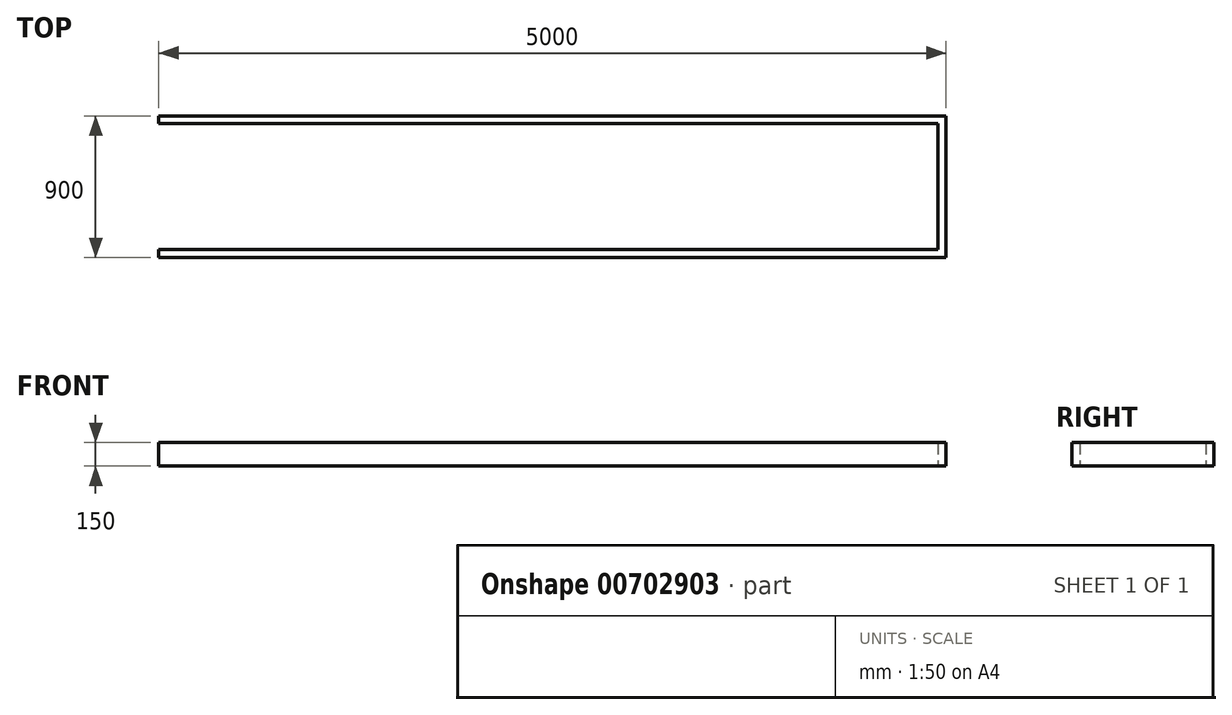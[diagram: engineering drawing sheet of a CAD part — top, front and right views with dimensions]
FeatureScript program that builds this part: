
annotation { "Feature Type Name" : "Feature", "Feature Type Description" : "" }
export const myFeature = defineFeature(function(context is Context, id is Id, definition is map)
    precondition{}
    {
        {
            var Q0;
            Q0=qCreatedBy(makeId("Top.planeOp"),FACE);
            var sketch = newSketch(context, id + "F0", { "sketchPlane" : qUnion([Q0])});
            skLineSegment(sketch, "E0.bottom", {"start": v(0, 0) * mm, "end": v(5000, 0) * mm});
            skLineSegment(sketch, "E0.top", {"start": v(0, -50) * mm, "end": v(5000, -50) * mm});
            skLineSegment(sketch, "E0.left", {"start": v(0, 0) * mm, "end": v(0, -50) * mm});
            skLineSegment(sketch, "E0.right", {"start": v(5000, 0) * mm, "end": v(5000, -50) * mm});
            skLineSegment(sketch, "E1.bottom", {"start": v(0, 4150) * mm, "end": v(5000, 4150) * mm});
            skLineSegment(sketch, "E1.top", {"start": v(0, -900) * mm, "end": v(5000, -900) * mm});
            skLineSegment(sketch, "E1.left", {"start": v(0, -850) * mm, "end": v(0, -900) * mm});
            skLineSegment(sketch, "E1.right", {"start": v(5000, -850) * mm, "end": v(5000, -900) * mm});
            skLineSegment(sketch, "E2.bottom", {"start": v(0, -50) * mm, "end": v(50, -50) * mm});
            skLineSegment(sketch, "E2.top", {"start": v(0, -850) * mm, "end": v(50, -850) * mm});
            skLineSegment(sketch, "E2.left", {"start": v(0, -50) * mm, "end": v(0, -850) * mm});
            skLineSegment(sketch, "E2.right", {"start": v(50, -50) * mm, "end": v(50, -850) * mm});
            skLineSegment(sketch, "E3.bottom", {"start": v(408.44, 5081.05) * mm, "end": v(458.44, 5081.05) * mm});
            skLineSegment(sketch, "E3.top", {"start": v(408.44, 4281.05) * mm, "end": v(458.44, 4281.05) * mm});
            skLineSegment(sketch, "E3.left", {"start": v(408.44, 5081.05) * mm, "end": v(408.44, 4281.05) * mm});
            skLineSegment(sketch, "E3.right", {"start": v(458.44, 5081.05) * mm, "end": v(458.44, 4281.05) * mm});
            skLineSegment(sketch, "E4", {"start": v(5000, -850) * mm, "end": v(0, -850) * mm});
            skLineSegment(sketch, "E5", {"start": v(5000, -50) * mm, "end": v(5000, -850) * mm});
            skLineSegment(sketch, "E6", {"start": v(5000, -850) * mm, "end": v(4950, -850) * mm});
            skLineSegment(sketch, "E7", {"start": v(4950, -850) * mm, "end": v(4950, -50) * mm});
            skLineSegment(sketch, "E8", {"start": v(4950, -50) * mm, "end": v(5000, -50) * mm});
            skLineSegment(sketch, "E9", {"start": v(4950, -450) * mm, "end": v(4950, -500) * mm});
            skSolve(sketch);
        }
        {
            var Q0;
            Q0=makeQuery(id+"F0.imprint","IMPRINT",FACE,{"disambiguationData":[TD([[makeQuery(id+"F0.imprint","IMPRINT",EDGE,{"derivedFrom":sQuery(id+"F0.wireOp",EDGE,"E0.bottom")}),-1.0]])]});
            var Q1;
            Q1=makeQuery(id+"F0.imprint","IMPRINT",FACE,{"disambiguationData":[TD([[makeQuery(id+"F0.imprint","IMPRINT",EDGE,{"derivedFrom":sQuery(id+"F0.wireOp",EDGE,"E2.bottom")}),-1.0]])]});
            var Q2;
            Q2=makeQuery(id+"F0.imprint","IMPRINT",FACE,{"disambiguationData":[TD([[makeQuery(id+"F0.imprint","IMPRINT",EDGE,{"derivedFrom":sQuery(id+"F0.wireOp",EDGE,"E1.top")}),1.0]])]});
            var Q3;
            Q3=makeQuery(id+"F0.imprint","IMPRINT",FACE,{"disambiguationData":[TD([[makeQuery(id+"F0.imprint","IMPRINT",EDGE,{"derivedFrom":sQuery(id+"F0.wireOp",EDGE,"E5")}),-1.0]])]});
            extrude(context, id + "F1", {"entities" : qUnion([Q0, Q1, Q2, Q3]), "depth" : 150 * mm, "offsetDistance" : 25 * mm});
        }
    });
